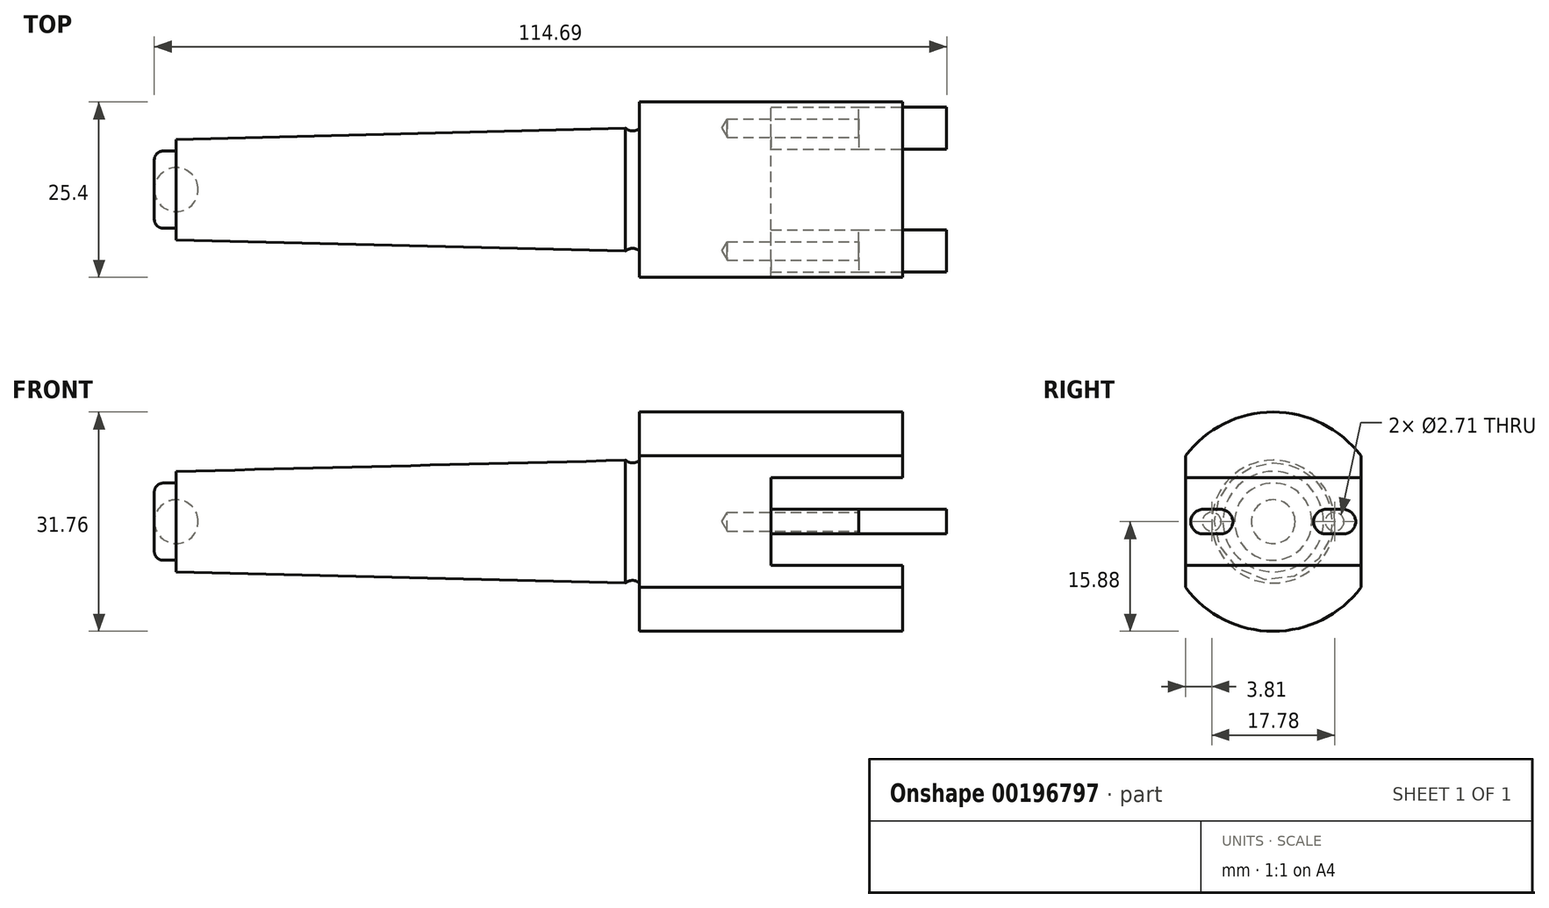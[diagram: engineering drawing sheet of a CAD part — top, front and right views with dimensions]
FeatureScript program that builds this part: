
annotation { "Feature Type Name" : "Feature", "Feature Type Description" : "" }
export const myFeature = defineFeature(function(context is Context, id is Id, definition is map)
    precondition{}
    {
        {
            var Q0;
            Q0=qCreatedBy(makeId("Front.planeOp"),FACE);
            var sketch = newSketch(context, id + "F0", { "sketchPlane" : qUnion([Q0])});
            skLineSegment(sketch, "E0", {"start": v(0, 0) * mm, "end": v(65.02, 0) * mm});
            skLineSegment(sketch, "E1", {"start": v(65.02, 0) * mm, "end": v(65.02, 8.9) * mm});
            skLineSegment(sketch, "E2", {"start": v(65.02, 8.9) * mm, "end": v(0, 7.27) * mm});
            skLineSegment(sketch, "E3", {"start": v(0, 7.27) * mm, "end": v(0, 0) * mm});
            skLineSegment(sketch, "E4.0", {"start": v(67.06, 0) * mm, "end": v(67.06, 8.9) * mm});
            skLineSegment(sketch, "E5", {"start": v(67.06, 8.9) * mm, "end": v(67.06, 15.87) * mm});
            skLineSegment(sketch, "E6", {"start": v(67.06, 15.87) * mm, "end": v(105.16, 15.87) * mm});
            skLineSegment(sketch, "E7", {"start": v(105.16, 15.87) * mm, "end": v(105.16, 0) * mm});
            skLineSegment(sketch, "E8", {"start": v(105.16, 0) * mm, "end": v(67.06, 0) * mm});
            skLineSegment(sketch, "E9", {"start": v(65.02, 0) * mm, "end": v(67.06, 0) * mm});
            skCircle(sketch, "E10", {"center": v(66.04, 10.03) * mm, "radius": 1.52 * mm});
            skPoint(sketch, "E10.centerSnap0", {"position": v(66.04, 0) * mm});
            skLineSegment(sketch, "E11", {"start": v(0, 0) * mm, "end": v(-3.18, 0) * mm});
            skLineSegment(sketch, "E12", {"start": v(-3.18, 0) * mm, "end": v(-3.18, 4.32) * mm});
            skLineSegment(sketch, "E13", {"start": v(-1.9, 5.59) * mm, "end": v(0, 5.59) * mm});
            skPoint(sketch, "E14.visualSharp", {"position": v(105.16, 15.87) * mm});
            skPoint(sketch, "E15.visualSharp", {"position": v(-3.18, 5.59) * mm});
            skArc(sketch, "E15.filletArc", {"start": v(-1.9, 5.59) * mm, "mid": v(-2.8, 5.22) * mm, "end": v(-3.18, 4.32) * mm});
            skSolve(sketch);
        }
        {
            var Q0;
            {var subQ3=sQuery(id+"F0.wireOp",EDGE,"E0");Q0=makeQuery(id+"F0.imprint","IMPRINT",FACE,{"disambiguationData":[TD([[makeQuery(id+"F0.imprint","IMPRINT",EDGE,{"derivedFrom":subQ3}),1.0]])]});}
            var Q1;
            {var subQ1=sQuery(id+"F0.wireOp",EDGE,"E11");Q1=makeQuery(id+"F0.imprint","IMPRINT",FACE,{"disambiguationData":[TD([[makeQuery(id+"F0.imprint","IMPRINT",EDGE,{"derivedFrom":subQ1}),-1.0]])]});}
            var Q2;
            {var subQ0=sQuery(id+"F0.wireOp",EDGE,"E1");Q2=makeQuery(id+"F0.imprint","IMPRINT",FACE,{"disambiguationData":[TD([[makeQuery(id+"F0.imprint","IMPRINT",EDGE,{"derivedFrom":subQ0}),-1.0]])]});}
            var Q3;
            {var subQ4=sQuery(id+"F0.wireOp",EDGE,"E4.0");Q3=makeQuery(id+"F0.imprint","IMPRINT",FACE,{"disambiguationData":[TD([[makeQuery(id+"F0.imprint","IMPRINT",EDGE,{"derivedFrom":subQ4}),-1.0]])]});}
            var Q4;
            {var subQ0=sQuery(id+"F0.wireOp",EDGE,"E10");var subQ1=sQuery(id+"F0.wireOp",EDGE,"E5");var subQ3=makeQuery(id+"F0.imprint","INTERSECT",VERTEX,{"derivedFrom":[subQ1,subQ0]});Q4=makeQuery(id+"F0.imprint","IMPRINT",FACE,{"disambiguationData":[TD([[makeQuery(id+"F0.imprint","IMPRINT",EDGE,{"disambiguationData":[TD([[subQ3,1.0]])],"derivedFrom":subQ1}),-1.0]])]});}
            var Q5;
            Q5=sQuery(id+"F0.wireOp",EDGE,"E0");
            revolve(context, id + "F1", {"entities" : qUnion([Q0, Q1, Q2, Q3, Q4]), "axis" : qUnion([Q5]), "revolveType" : RevolveType.FULL});
        }
        {
            var Q0;
            Q0=qCreatedBy(makeId("Front.planeOp"),FACE);
            var sketch = newSketch(context, id + "F2", { "sketchPlane" : qUnion([Q0])});
            skLineSegment(sketch, "E16.0", {"start": v(105.16, -15.87) * mm, "end": v(105.16, 15.87) * mm});
            skPoint(sketch, "E17", {"position": v(105.16, 0) * mm});
            skLineSegment(sketch, "E18", {"start": v(105.16, 6.35) * mm, "end": v(105.16, -6.35) * mm});
            skLineSegment(sketch, "E19.0", {"start": v(98.8, 6.35) * mm, "end": v(98.8, -6.35) * mm});
            skLineSegment(sketch, "E20", {"start": v(105.16, 6.35) * mm, "end": v(98.8, 6.35) * mm});
            skLineSegment(sketch, "E21", {"start": v(105.16, -6.35) * mm, "end": v(98.8, -6.35) * mm});
            skSolve(sketch);
        }
        {
            var Q0;
            {var subQ0=sQuery(id+"F2.wireOp",EDGE,"E18");Q0=makeQuery(id+"F2.imprint","IMPRINT",FACE,{"disambiguationData":[TD([[makeQuery(id+"F2.imprint","IMPRINT",EDGE,{"derivedFrom":subQ0}),-1.0]])]});}
            var Q1;
            {var subQ0=sQuery(id+"F2.wireOp",EDGE,"E19.0");Q1=makeQuery(id+"F2.imprint","IMPRINT",FACE,{"disambiguationData":[TD([[makeQuery(id+"F2.imprint","IMPRINT",EDGE,{"derivedFrom":subQ0}),1.0]])]});}
            extrude(context, id + "F3", {"entities" : qUnion([Q0, Q1]), "operationType" : NewBodyOperationType.REMOVE, "endBound" : BoundingType.SYMMETRIC, "oppositeDirection" : true, "depth" : 50.8 * mm});
        }
        {
            var Q0;
            Q0=makeQuery(id+"F3.boolean.opBoolean","SPLIT",FACE,{"disambiguationData":[TD([makeQuery(id+"F3.opExtrude","SWEPT_FACE",FACE,{"disambiguationData":[OSD([sQuery(id+"F2.wireOp",EDGE,"E20")])]})])],"derivedFrom":makeQuery(id+"F1.opRevolve","SWEPT_FACE",FACE,{"disambiguationData":[OSD([sQuery(id+"F0.wireOp",EDGE,"E7")])]})});
            var sketch = newSketch(context, id + "F4", { "sketchPlane" : qUnion([Q0])});
            skArc(sketch, "E22.0", {"start": v(-14.55, 6.35) * mm, "mid": v(0, 15.88) * mm, "end": v(14.55, 6.35) * mm});
            skArc(sketch, "E23.0", {"start": v(-14.55, 6.35) * mm, "mid": v(-15.87, 0) * mm, "end": v(-14.55, -6.35) * mm});
            skArc(sketch, "E24.0", {"start": v(14.55, -6.35) * mm, "mid": v(0, -15.87) * mm, "end": v(-14.55, -6.35) * mm});
            skArc(sketch, "E25.0", {"start": v(14.55, -6.35) * mm, "mid": v(15.87, 0) * mm, "end": v(14.55, 6.35) * mm});
            skLineSegment(sketch, "E26.bottom", {"start": v(12.7, 19.05) * mm, "end": v(-12.7, 19.05) * mm});
            skLineSegment(sketch, "E26.top", {"start": v(12.7, -19.05) * mm, "end": v(-12.7, -19.05) * mm});
            skLineSegment(sketch, "E26.left", {"start": v(12.7, 19.05) * mm, "end": v(12.7, -19.05) * mm});
            skLineSegment(sketch, "E26.right", {"start": v(-12.7, 19.05) * mm, "end": v(-12.7, -19.05) * mm});
            skSolve(sketch);
        }
        {
            var Q0;
            Q0=qCreatedBy(makeId("Front.planeOp"),FACE);
            var sketch = newSketch(context, id + "F5", { "sketchPlane" : qUnion([Q0])});
            skPoint(sketch, "E27.0", {"position": v(98.8, -6.35) * mm});
            skPoint(sketch, "E28.0", {"position": v(98.8, 6.35) * mm});
            skLineSegment(sketch, "E29.bottom", {"start": v(98.8, -6.35) * mm, "end": v(111.5, -6.35) * mm});
            skLineSegment(sketch, "E29.top", {"start": v(98.8, 6.35) * mm, "end": v(111.5, 6.35) * mm});
            skLineSegment(sketch, "E29.left", {"start": v(98.8, -6.35) * mm, "end": v(98.8, 6.35) * mm});
            skLineSegment(sketch, "E29.right", {"start": v(111.5, -6.35) * mm, "end": v(111.5, 6.35) * mm});
            skLineSegment(sketch, "E30", {"start": v(111.5, 3.68) * mm, "end": v(111.5, -3.68) * mm});
            skPoint(sketch, "E31", {"position": v(111.5, 0) * mm});
            skLineSegment(sketch, "E32", {"start": v(111.5, 3.68) * mm, "end": v(107.88, 1.59) * mm});
            skLineSegment(sketch, "E33", {"start": v(107.88, 1.59) * mm, "end": v(104.7, 1.59) * mm});
            skLineSegment(sketch, "E34", {"start": v(104.7, 1.59) * mm, "end": v(103.96, 0) * mm});
            skLineSegment(sketch, "E35", {"start": v(103.96, 0) * mm, "end": v(111.5, 0) * mm});
            skSolve(sketch);
        }
        {
            var Q0;
            {var subQ0=sQuery(id+"F4.wireOp",EDGE,"E23.0");Q0=makeQuery(id+"F4.imprint","IMPRINT",FACE,{"disambiguationData":[TD([[makeQuery(id+"F4.imprint","IMPRINT",EDGE,{"derivedFrom":subQ0}),1.0]])]});}
            var Q1;
            {var subQ0=sQuery(id+"F4.wireOp",EDGE,"E22.0");var subQ3=sQuery(id+"F4.wireOp",EDGE,"E26.right");var subQ4=makeQuery(id+"F4.imprint","INTERSECT",VERTEX,{"derivedFrom":[subQ0,subQ3]});Q1=makeQuery(id+"F4.imprint","IMPRINT",FACE,{"disambiguationData":[TD([[makeQuery(id+"F4.imprint","IMPRINT",EDGE,{"disambiguationData":[TD([[subQ4,-1.0]])],"derivedFrom":subQ3}),-1.0]])]});}
            var Q2;
            {var subQ0=sQuery(id+"F4.wireOp",EDGE,"E25.0");Q2=makeQuery(id+"F4.imprint","IMPRINT",FACE,{"disambiguationData":[TD([[makeQuery(id+"F4.imprint","IMPRINT",EDGE,{"derivedFrom":subQ0}),1.0]])]});}
            var Q3;
            {var subQ0=sQuery(id+"F4.wireOp",EDGE,"E22.0");var subQ3=sQuery(id+"F4.wireOp",EDGE,"E26.left");var subQ4=makeQuery(id+"F4.imprint","INTERSECT",VERTEX,{"derivedFrom":[subQ0,subQ3]});Q3=makeQuery(id+"F4.imprint","IMPRINT",FACE,{"disambiguationData":[TD([[makeQuery(id+"F4.imprint","IMPRINT",EDGE,{"disambiguationData":[TD([[subQ4,-1.0]])],"derivedFrom":subQ3}),1.0]])]});}
            extrude(context, id + "F6", {"entities" : qUnion([Q0, Q1, Q2, Q3]), "operationType" : NewBodyOperationType.REMOVE, "oppositeDirection" : true, "depth" : 38.1 * mm});
        }
        {
            var Q0;
            Q0=makeQuery(id+"F3.boolean.opBoolean","COPY",FACE,{"derivedFrom":makeQuery(id+"F3.opExtrude","SWEPT_FACE",FACE,{"disambiguationData":[OSD([sQuery(id+"F2.wireOp",EDGE,"E19.0")])]})});
            var sketch = newSketch(context, id + "F7", { "sketchPlane" : qUnion([Q0])});
            skLineSegment(sketch, "E36", {"start": v(-8.9, 0) * mm, "end": v(8.9, 0) * mm});
            skSolve(sketch);
        }
        {
            var Q0;
            Q0=sQuery(id+"F7.wireOp",VERTEX,"E36.start");
            var Q1;
            Q1=sQuery(id+"F7.wireOp",VERTEX,"E36.end");
            var Q2;
            Q2=makeQuery(id+"F1.opRevolve","SWEPT_BODY",BODY,{"disambiguationData":[OSD([sQuery(id+"F0.wireOp",EDGE,"E0"),sQuery(id+"F0.wireOp",EDGE,"E2"),sQuery(id+"F0.wireOp",EDGE,"E3"),sQuery(id+"F0.wireOp",EDGE,"E5"),sQuery(id+"F0.wireOp",EDGE,"E6"),sQuery(id+"F0.wireOp",EDGE,"E7"),sQuery(id+"F0.wireOp",EDGE,"E8"),sQuery(id+"F0.wireOp",EDGE,"E9"),sQuery(id+"F0.wireOp",EDGE,"E10"),sQuery(id+"F0.wireOp",EDGE,"E11"),sQuery(id+"F0.wireOp",EDGE,"E12"),sQuery(id+"F0.wireOp",EDGE,"E13"),sQuery(id+"F0.wireOp",EDGE,"E15.filletArc")])]});
            hole(context, id + "F8", {"style" : HoleStyle.SIMPLE, "endStyle" : HoleEndStyle.BLIND, "standardTappedOrClearance" : lookupTablePath({ "standard" : "ANSI", "engagement" : "75%", "pitch" : "32 tpi", "size" : "#6", "type" : "Tapped" }), "standardBlindInLast" : lookupTablePath({ "standard" : "ANSI", "engagement" : "75%", "pitch" : "32 tpi", "size" : "#6", "type" : "Tapped" }), "holeDiameter" : 2.7 * mm, "holeDepth" : 19.05 * mm, "locations" : qUnion([Q0, Q1]), "scope" : qUnion([Q2]), "majorDiameter" : 3.5 * mm});
        }
        {
            var Q0;
            Q0=makeQuery(id+"F5.imprint","IMPRINT",FACE,{"disambiguationData":[TD([[makeQuery(id+"F5.imprint","IMPRINT",EDGE,{"derivedFrom":sQuery(id+"F5.wireOp",EDGE,"E29.bottom")}),1.0]])]});
            var Q1;
            {var subQ0=sQuery(id+"F5.wireOp",EDGE,"E32");Q1=makeQuery(id+"F5.imprint","IMPRINT",FACE,{"disambiguationData":[TD([[makeQuery(id+"F5.imprint","IMPRINT",EDGE,{"derivedFrom":subQ0}),1.0]])]});}
            extrude(context, id + "F9", {"entities" : qUnion([Q0, Q1]), "endBound" : BoundingType.SYMMETRIC, "depth" : 25.4 * mm});
        }
        {
            var Q0;
            Q0=makeQuery(id+"F9.opExtrude","SWEPT_FACE",FACE,{"disambiguationData":[OSD([sQuery(id+"F5.wireOp",EDGE,"E29.right")])]});
            var sketch = newSketch(context, id + "F10", { "sketchPlane" : qUnion([Q0])});
            skPoint(sketch, "E37.0", {"position": v(-8.9, 0) * mm});
            skPoint(sketch, "E38.0", {"position": v(8.9, 0) * mm});
            skPoint(sketch, "E39", {"position": v(-12.7, 0) * mm});
            skLineSegment(sketch, "E40", {"start": v(7.62, 0) * mm, "end": v(10.16, 0) * mm});
            skArc(sketch, "E41.0.startCap", {"start": v(7.62, -1.78) * mm, "mid": v(5.84, 0) * mm, "end": v(7.62, 1.78) * mm});
            skArc(sketch, "E41.0.endCap", {"start": v(10.16, 1.78) * mm, "mid": v(11.94, 0) * mm, "end": v(10.16, -1.78) * mm});
            skLineSegment(sketch, "E41.0.left", {"start": v(7.62, 1.78) * mm, "end": v(10.16, 1.78) * mm});
            skLineSegment(sketch, "E41.0.right", {"start": v(7.62, -1.78) * mm, "end": v(10.16, -1.78) * mm});
            skLineSegment(sketch, "E42", {"start": v(-10.16, 0) * mm, "end": v(-7.62, 0) * mm});
            skArc(sketch, "E43.0.startCap", {"start": v(-10.16, -1.78) * mm, "mid": v(-11.94, 0) * mm, "end": v(-10.16, 1.78) * mm});
            skArc(sketch, "E43.0.endCap", {"start": v(-7.62, 1.78) * mm, "mid": v(-5.84, 0) * mm, "end": v(-7.62, -1.78) * mm});
            skLineSegment(sketch, "E43.0.left", {"start": v(-10.16, 1.78) * mm, "end": v(-7.62, 1.78) * mm});
            skLineSegment(sketch, "E43.0.right", {"start": v(-10.16, -1.78) * mm, "end": v(-7.62, -1.78) * mm});
            skSolve(sketch);
        }
        {
            var Q0;
            Q0=makeQuery(id+"F10.imprint","IMPRINT",FACE,{"disambiguationData":[TD([[makeQuery(id+"F10.imprint","IMPRINT",EDGE,{"derivedFrom":sQuery(id+"F10.wireOp",EDGE,"0261e142-935a-4c9b-ab3e-8d91aa75bd70.0.startCap")}),-1.0]])]});
            var Q1;
            Q1=makeQuery(id+"F10.imprint","IMPRINT",FACE,{"disambiguationData":[TD([[makeQuery(id+"F10.imprint","IMPRINT",EDGE,{"derivedFrom":sQuery(id+"F10.wireOp",EDGE,"E41.0.startCap")}),-1.0]])]});
            var Q2;
            Q2=makeQuery(id+"F10.imprint","IMPRINT",FACE,{"disambiguationData":[TD([[makeQuery(id+"F10.imprint","IMPRINT",EDGE,{"derivedFrom":sQuery(id+"F10.wireOp",EDGE,"E43.0.startCap")}),-1.0]])]});
            extrude(context, id + "F11", {"entities" : qUnion([Q0, Q1, Q2]), "operationType" : NewBodyOperationType.REMOVE, "oppositeDirection" : true, "depth" : 25.4 * mm});
        }
        {
            var Q0;
            {var subQ0=sQuery(id+"F5.wireOp",EDGE,"E32");Q0=makeQuery(id+"F5.imprint","IMPRINT",FACE,{"disambiguationData":[TD([[makeQuery(id+"F5.imprint","IMPRINT",EDGE,{"derivedFrom":subQ0}),1.0]])]});}
            var Q1;
            Q1=sQuery(id+"F5.wireOp",EDGE,"E35");
            revolve(context, id + "F12", {"operationType" : NewBodyOperationType.REMOVE, "entities" : qUnion([Q0]), "axis" : qUnion([Q1]), "revolveType" : RevolveType.FULL, "oppositeDirection" : true});
        }
        {
            var Q0;
            Q0=makeQuery(id+"F9.opExtrude","SWEPT_FACE",FACE,{"disambiguationData":[OSD([sQuery(id+"F5.wireOp",EDGE,"E29.right"),sQuery(id+"F5.wireOp",EDGE,"E30")])]});
            var sketch = newSketch(context, id + "F13", { "sketchPlane" : qUnion([Q0])});
            skLineSegment(sketch, "E44.0.0", {"start": v(12.7, -6.35) * mm, "end": v(12.7, 6.35) * mm});
            skLineSegment(sketch, "E44.0.1", {"start": v(12.7, 6.35) * mm, "end": v(-12.7, 6.35) * mm});
            skLineSegment(sketch, "E44.0.2", {"start": v(-12.7, 6.35) * mm, "end": v(-12.7, -6.35) * mm});
            skLineSegment(sketch, "E44.0.3", {"start": v(-12.7, -6.35) * mm, "end": v(12.7, -6.35) * mm});
            skLineSegment(sketch, "E45", {"start": v(4.7, 6.35) * mm, "end": v(4.7, -6.35) * mm});
            skLineSegment(sketch, "E46", {"start": v(-4.7, 6.35) * mm, "end": v(-4.7, -6.35) * mm});
            skSolve(sketch);
        }
        {
            var Q0;
            {var subQ2=sQuery(id+"F13.wireOp",EDGE,"E44.0.0");Q0=makeQuery(id+"F13.imprint","IMPRINT",FACE,{"disambiguationData":[TD([[makeQuery(id+"F13.imprint","IMPRINT",EDGE,{"derivedFrom":subQ2}),1.0]])]});}
            var Q1;
            {var subQ1=sQuery(id+"F13.wireOp",EDGE,"E44.0.2");Q1=makeQuery(id+"F13.imprint","IMPRINT",FACE,{"disambiguationData":[TD([[makeQuery(id+"F13.imprint","IMPRINT",EDGE,{"derivedFrom":subQ1}),-1.0]])]});}
            extrude(context, id + "F14", {"entities" : qUnion([Q0, Q1]), "operationType" : NewBodyOperationType.REMOVE, "oppositeDirection" : true, "depth" : 3.56 * mm});
        }
        {
            var Q0;
            Q0=qCreatedBy(makeId("Front.planeOp"),FACE);
            var sketch = newSketch(context, id + "F15", { "sketchPlane" : qUnion([Q0])});
            skCircle(sketch, "E47", {"center": v(0, 0) * mm, "radius": 3.18 * mm});
            skLineSegment(sketch, "E48", {"start": v(-3.17, 0) * mm, "end": v(3.17, 0) * mm});
            skSolve(sketch);
        }
        {
            var Q0;
            {var subQ0=sQuery(id+"F15.wireOp",EDGE,"E48");Q0=makeQuery(id+"F15.imprint","IMPRINT",FACE,{"disambiguationData":[TD([[makeQuery(id+"F15.imprint","IMPRINT",EDGE,{"derivedFrom":subQ0}),1.0]])]});}
            var Q1;
            Q1=sQuery(id+"F15.wireOp",EDGE,"E48");
            revolve(context, id + "F16", {"entities" : qUnion([Q0]), "axis" : qUnion([Q1]), "revolveType" : RevolveType.FULL});
        }
    });
